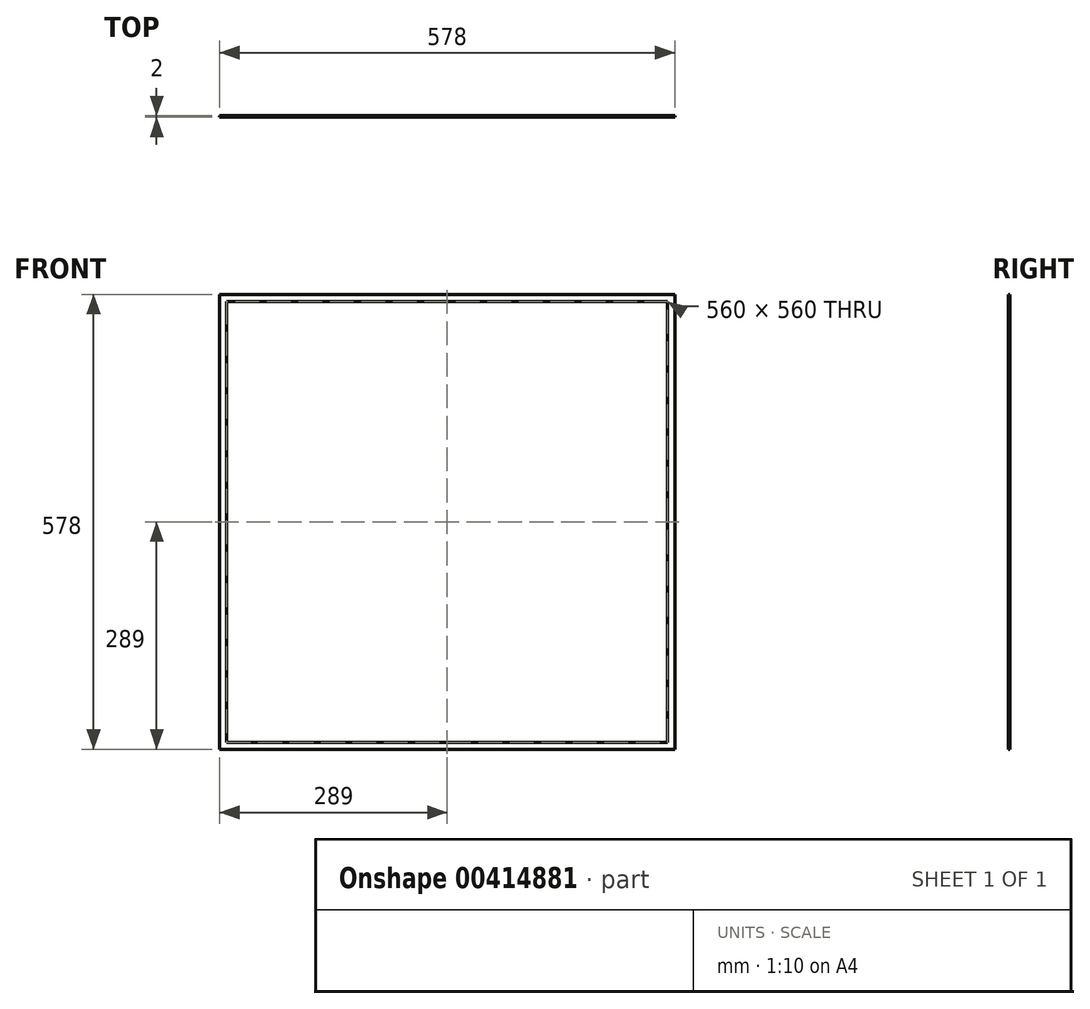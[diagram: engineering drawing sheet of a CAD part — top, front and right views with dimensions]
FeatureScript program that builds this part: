
annotation { "Feature Type Name" : "Feature", "Feature Type Description" : "" }
export const myFeature = defineFeature(function(context is Context, id is Id, definition is map)
    precondition{}
    {
        {
            var Q0;
            Q0=qCreatedBy(makeId("Front.planeOp"),FACE);
            var sketch = newSketch(context, id + "F0", { "sketchPlane" : qUnion([Q0])});
            skLineSegment(sketch, "E0.bottom", {"start": v(-289, 289) * mm, "end": v(289, 289) * mm});
            skLineSegment(sketch, "E0.top", {"start": v(-289, -289) * mm, "end": v(289, -289) * mm});
            skLineSegment(sketch, "E0.left", {"start": v(-289, 289) * mm, "end": v(-289, -289) * mm});
            skLineSegment(sketch, "E0.right", {"start": v(289, 289) * mm, "end": v(289, -289) * mm});
            skLineSegment(sketch, "E1.bottom", {"start": v(-280, 280) * mm, "end": v(280, 280) * mm});
            skLineSegment(sketch, "E1.top", {"start": v(-280, -280) * mm, "end": v(280, -280) * mm});
            skLineSegment(sketch, "E1.left", {"start": v(-280, 280) * mm, "end": v(-280, -280) * mm});
            skLineSegment(sketch, "E1.right", {"start": v(280, 280) * mm, "end": v(280, -280) * mm});
            skLineSegment(sketch, "E2", {"start": v(-280, 280) * mm, "end": v(280, -280) * mm, "construction": true});
            skSolve(sketch);
        }
        {
            var Q0;
            Q0=makeQuery(id+"F0.imprint","IMPRINT",FACE,{"disambiguationData":[TD([[makeQuery(id+"F0.imprint","IMPRINT",EDGE,{"derivedFrom":sQuery(id+"F0.wireOp",EDGE,"E0.bottom")}),-1.0]])]});
            extrude(context, id + "F1", {"entities" : qUnion([Q0]), "depth" : 2 * mm});
        }
    });
